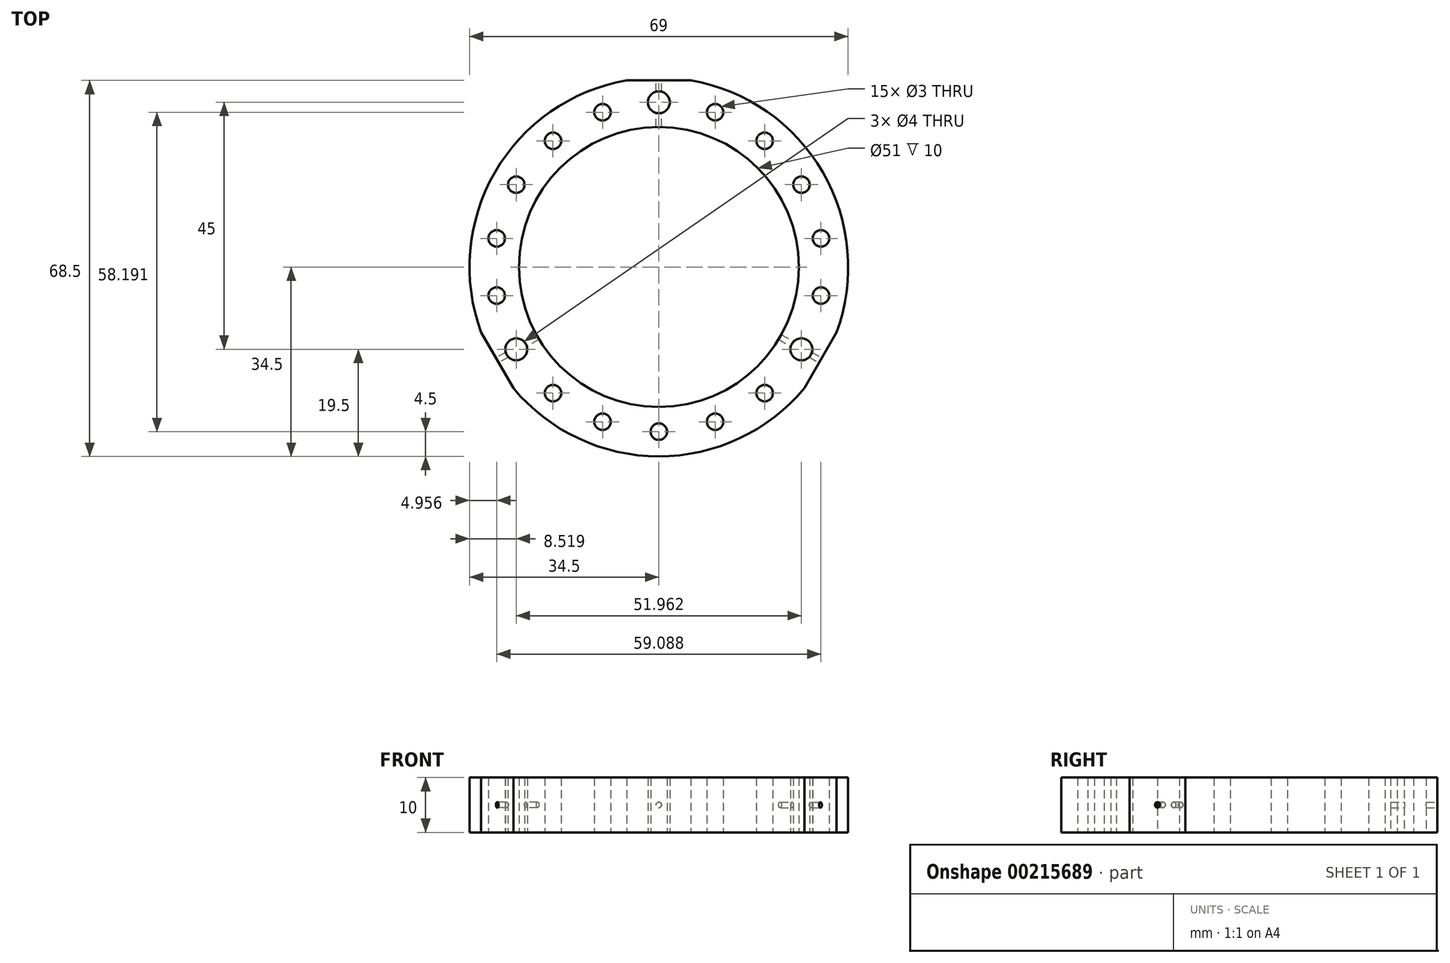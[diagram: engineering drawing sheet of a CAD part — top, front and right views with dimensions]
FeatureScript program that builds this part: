
annotation { "Feature Type Name" : "Feature", "Feature Type Description" : "" }
export const myFeature = defineFeature(function(context is Context, id is Id, definition is map)
    precondition{}
    {
        {
            var Q0;
            Q0=qCreatedBy(makeId("Top.planeOp"),FACE);
            var sketch = newSketch(context, id + "F0", { "sketchPlane" : qUnion([Q0])});
            skCircle(sketch, "E0", {"center": v(0, 0) * mm, "radius": 30 * mm, "construction": true});
            skLineSegment(sketch, "E1", {"start": v(0, 30) * mm, "end": v(-25.98, -15) * mm, "construction": true});
            skLineSegment(sketch, "E2", {"start": v(-25.98, -15) * mm, "end": v(25.98, -15) * mm, "construction": true});
            skLineSegment(sketch, "E3", {"start": v(25.98, -15) * mm, "end": v(0, 30) * mm, "construction": true});
            skCircle(sketch, "E4", {"center": v(0, 30) * mm, "radius": 2 * mm});
            skCircle(sketch, "E5", {"center": v(-25.98, -15) * mm, "radius": 2 * mm});
            skCircle(sketch, "E6", {"center": v(25.98, -15) * mm, "radius": 2 * mm});
            skArc(sketch, "E7", {"start": v(-26.52, -22.07) * mm, "mid": v(0, -34.5) * mm, "end": v(26.52, -22.07) * mm});
            skCircle(sketch, "E8", {"center": v(0, 30) * mm, "radius": 1.5 * mm});
            skCircle(sketch, "E9.1.0", {"center": v(10.26, 28.2) * mm, "radius": 1.5 * mm});
            skCircle(sketch, "E9.2.0", {"center": v(19.28, 22.98) * mm, "radius": 1.5 * mm});
            skCircle(sketch, "E9.3.0", {"center": v(25.98, 15) * mm, "radius": 1.5 * mm});
            skCircle(sketch, "E9.4.0", {"center": v(29.54, 5.2) * mm, "radius": 1.5 * mm});
            skCircle(sketch, "E9.5.0", {"center": v(29.54, -5.2) * mm, "radius": 1.5 * mm});
            skCircle(sketch, "E9.6.0", {"center": v(25.98, -15) * mm, "radius": 1.5 * mm});
            skCircle(sketch, "E9.7.0", {"center": v(19.28, -22.98) * mm, "radius": 1.5 * mm});
            skCircle(sketch, "E9.8.0", {"center": v(10.26, -28.2) * mm, "radius": 1.5 * mm});
            skCircle(sketch, "E9.9.0", {"center": v(0, -30) * mm, "radius": 1.5 * mm});
            skCircle(sketch, "E9.10.0", {"center": v(-10.26, -28.2) * mm, "radius": 1.5 * mm});
            skCircle(sketch, "E9.11.0", {"center": v(-19.28, -22.98) * mm, "radius": 1.5 * mm});
            skCircle(sketch, "E9.12.0", {"center": v(-25.98, -15) * mm, "radius": 1.5 * mm});
            skCircle(sketch, "E9.13.0", {"center": v(-29.54, -5.2) * mm, "radius": 1.5 * mm});
            skCircle(sketch, "E9.14.0", {"center": v(-29.54, 5.2) * mm, "radius": 1.5 * mm});
            skCircle(sketch, "E9.15.0", {"center": v(-25.98, 15) * mm, "radius": 1.5 * mm});
            skCircle(sketch, "E9.16.0", {"center": v(-19.28, 22.98) * mm, "radius": 1.5 * mm});
            skCircle(sketch, "E9.17.0", {"center": v(-10.26, 28.2) * mm, "radius": 1.5 * mm});
            skLineSegment(sketch, "E9.anchor1", {"start": v(0, 0) * mm, "end": v(0, 30) * mm, "construction": true});
            skLineSegment(sketch, "E9.anchor2", {"start": v(0, 0) * mm, "end": v(0, 30) * mm, "construction": true});
            skCircle(sketch, "E10", {"center": v(0, 0) * mm, "radius": 25.5 * mm});
            skLineSegment(sketch, "E11", {"start": v(0, 0) * mm, "end": v(-25.98, -15) * mm, "construction": true});
            skLineSegment(sketch, "E12", {"start": v(0, 0) * mm, "end": v(25.98, -15) * mm, "construction": true});
            skLineSegment(sketch, "E13", {"start": v(-5.85, 34) * mm, "end": v(5.85, 34) * mm});
            skLineSegment(sketch, "E14", {"start": v(-32.37, -11.93) * mm, "end": v(-26.52, -22.07) * mm});
            skLineSegment(sketch, "E15", {"start": v(32.37, -11.93) * mm, "end": v(26.52, -22.07) * mm});
            skArc(sketch, "E16.trimOffspring", {"start": v(32.37, -11.93) * mm, "mid": v(29.88, 17.25) * mm, "end": v(5.85, 34) * mm});
            skArc(sketch, "E17.trimOffspring", {"start": v(-5.85, 34) * mm, "mid": v(-29.88, 17.25) * mm, "end": v(-32.37, -11.93) * mm});
            skSolve(sketch);
        }
        {
            var Q0;
            Q0=qSketchRegion(id+"F0",true);
            extrude(context, id + "F1", {"entities" : qUnion([Q0]), "depth" : 10 * mm});
        }
        {
            var Q0;
            Q0=makeQuery(id+"F1.opExtrude","SWEPT_FACE",FACE,{"disambiguationData":[OSD([sQuery(id+"F0.wireOp",EDGE,"E14")])]});
            var sketch = newSketch(context, id + "F2", { "sketchPlane" : qUnion([Q0])});
            skCircle(sketch, "E18", {"center": v(0, 5) * mm, "radius": 0.5 * mm});
            skPoint(sketch, "E18.centerSnap0", {"position": v(-5.85, 5) * mm});
            skSolve(sketch);
        }
        {
            var Q0;
            Q0 = qSketchRegion(id + "F2", true);
            extrude(context, id + "F3", {"entities" : qUnion([Q0]), "operationType" : NewBodyOperationType.REMOVE, "oppositeDirection" : true, "depth" : 15 * mm});
        }
        {
            var Q0;
            Q0=makeQuery(id+"F1.opExtrude","SWEPT_FACE",FACE,{"disambiguationData":[OSD([sQuery(id+"F0.wireOp",EDGE,"E15")])]});
            var sketch = newSketch(context, id + "F4", { "sketchPlane" : qUnion([Q0])});
            skCircle(sketch, "E19", {"center": v(0, 5) * mm, "radius": 0.5 * mm});
            skPoint(sketch, "E19.centerSnap0", {"position": v(-5.85, 5) * mm});
            skSolve(sketch);
        }
        {
            var Q0;
            Q0 = qSketchRegion(id + "F4", true);
            extrude(context, id + "F5", {"entities" : qUnion([Q0]), "operationType" : NewBodyOperationType.REMOVE, "oppositeDirection" : true, "depth" : 15 * mm});
        }
        {
            var Q0;
            Q0=makeQuery(id+"F1.opExtrude","SWEPT_FACE",FACE,{"disambiguationData":[OSD([sQuery(id+"F0.wireOp",EDGE,"E13")])]});
            var sketch = newSketch(context, id + "F6", { "sketchPlane" : qUnion([Q0])});
            skCircle(sketch, "E20", {"center": v(0, 5) * mm, "radius": 0.5 * mm});
            skPoint(sketch, "E20.centerSnap0", {"position": v(-5.85, 5) * mm});
            skSolve(sketch);
        }
        {
            var Q0;
            Q0 = qSketchRegion(id + "F6", true);
            extrude(context, id + "F7", {"entities" : qUnion([Q0]), "operationType" : NewBodyOperationType.REMOVE, "oppositeDirection" : true, "depth" : 15 * mm});
        }
    });
